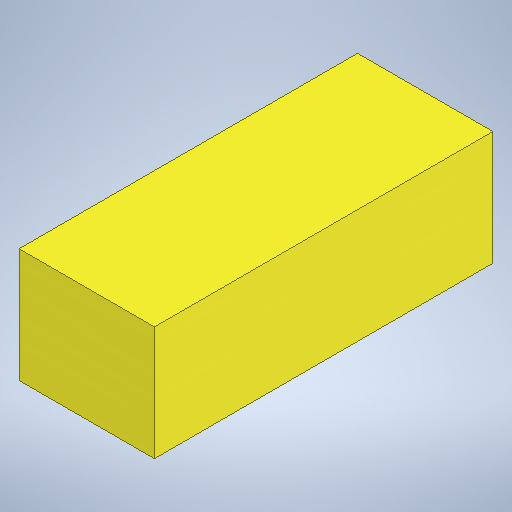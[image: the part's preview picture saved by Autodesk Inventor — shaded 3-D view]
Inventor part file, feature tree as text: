
AUTODESK INVENTOR PART (.ipt)
format: ipt  version: 2025.1 (Build 291241020, 241B)  size: 176,128 bytes
history: native  units: in
note: dims shown in document units (in); Inventor stores cm internally (conversion verified against a paired STEP export)
features: extrude x1, sketch x1
ambient origin geometry x8: Origin, YZ Plane, XZ Plane, XY Plane, X Axis, Y Axis, Z Axis, Center Point
bodies: Solid1 (feature_tree)
feature tree (2):
  extrude  "Extrusion1"  Depth=2.7559in
  sketch  "Sketch1"  dims[d0=6.8898in d1=2.7559in d2=2.3228in d3=0.0in]
